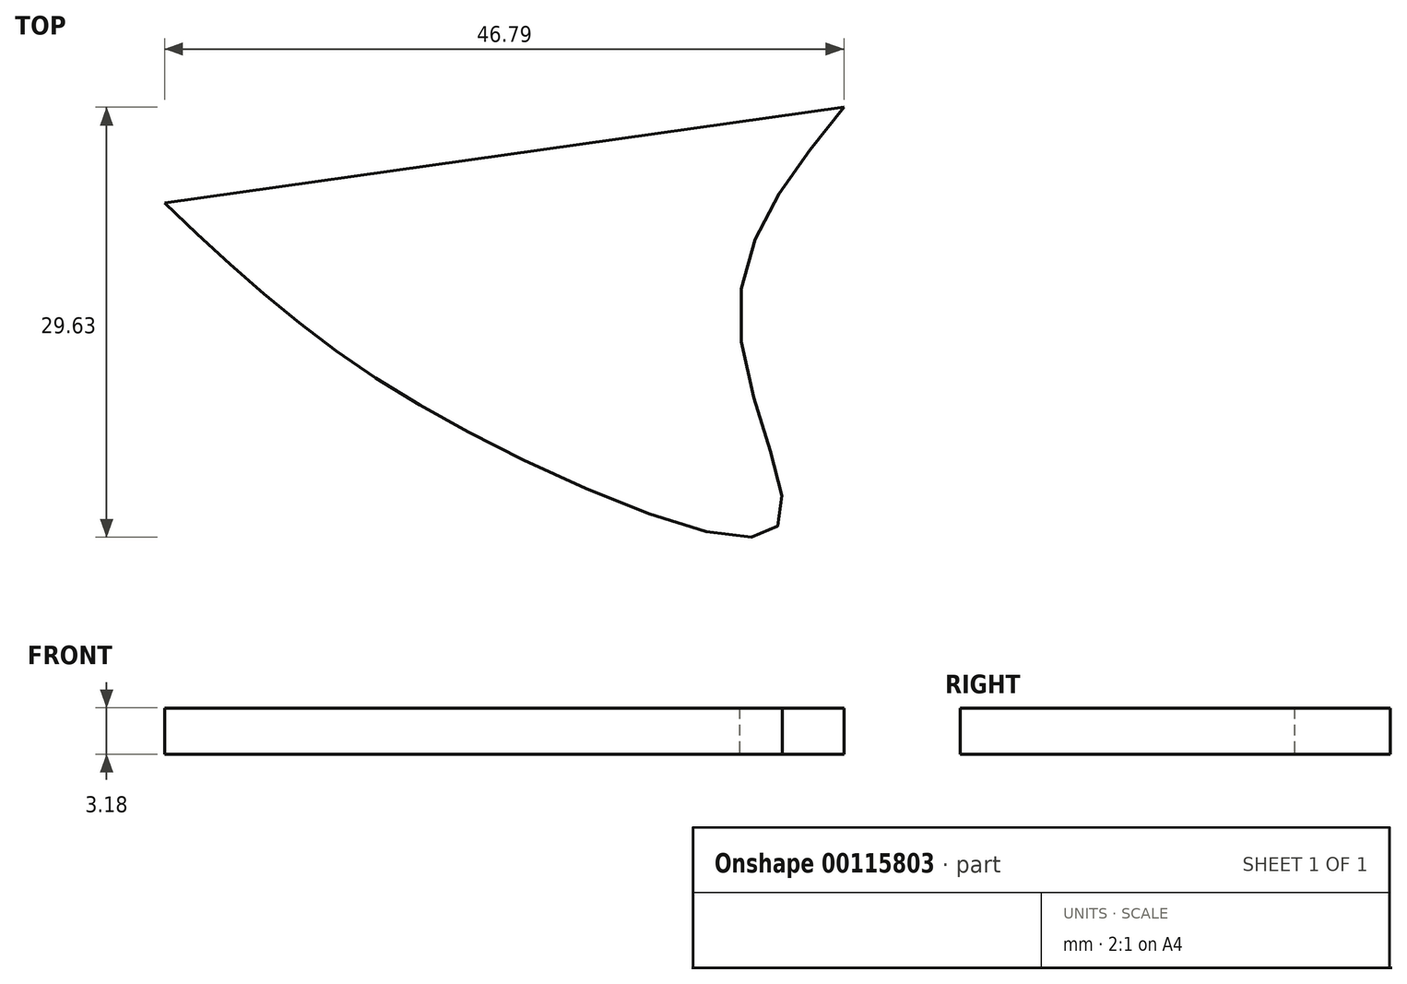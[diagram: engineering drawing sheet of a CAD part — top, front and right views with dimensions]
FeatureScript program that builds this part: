
annotation { "Feature Type Name" : "Feature", "Feature Type Description" : "" }
export const myFeature = defineFeature(function(context is Context, id is Id, definition is map)
    precondition{}
    {
        {
            var Q0;
            Q0=qCreatedBy(makeId("Top.planeOp"),FACE);
            var sketch = newSketch(context, id + "F0", { "sketchPlane" : qUnion([Q0])});
            skFitSpline(sketch, "E0", {"points": [v(-46.79, 8.57) * mm, v(-37.14, 0) * mm, v(-21.9, -9.2) * mm, v(-4.63, -13.78) * mm, v(-7.17, 0) * mm, v(0, 15.17) * mm], "startDerivative": vector(51.46, -48.74) * mm, "endDerivative": vector(54.94, 67.5) * mm});
            skLineSegment(sketch, "E1", {"start": v(-46.79, 8.57) * mm, "end": v(0, 15.17) * mm});
            skSolve(sketch);
        }
        {
            var Q0;
            Q0=makeQuery(id+"F0.imprint","IMPRINT",FACE,{"disambiguationData":[TD([[makeQuery(id+"F0.imprint","IMPRINT",EDGE,{"derivedFrom":sQuery(id+"F0.wireOp",EDGE,"E0")}),1.0]])]});
            extrude(context, id + "F1", {"entities" : qUnion([Q0]), "depth" : 3.17 * mm});
        }
    });
